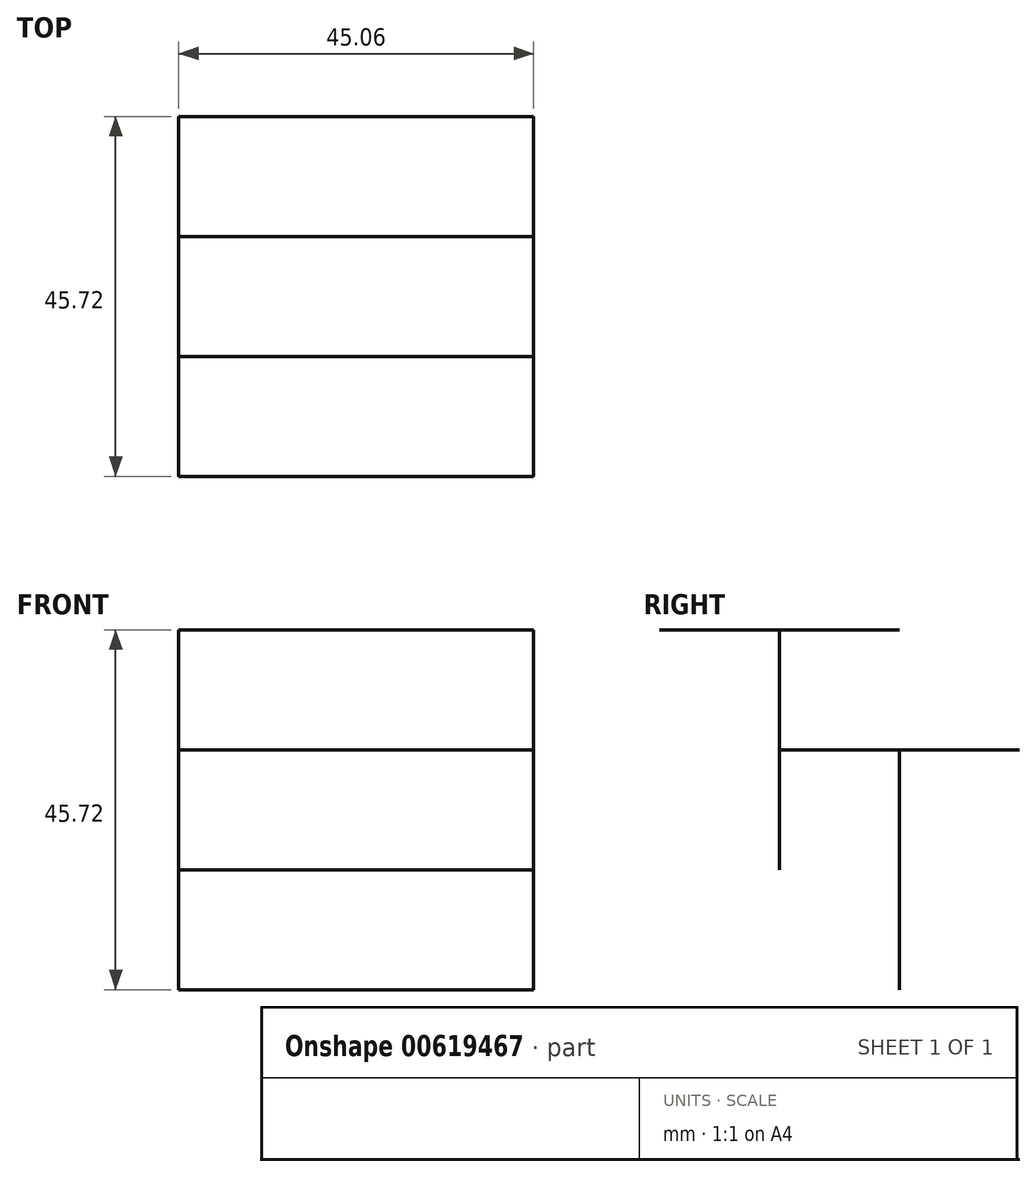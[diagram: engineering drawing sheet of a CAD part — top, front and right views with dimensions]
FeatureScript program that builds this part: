
annotation { "Feature Type Name" : "Feature", "Feature Type Description" : "" }
export const myFeature = defineFeature(function(context is Context, id is Id, definition is map)
    precondition{}
    {
        {
            var Q0;
            Q0=qCreatedBy(makeId("Front.planeOp"),FACE);
            var sketch = newSketch(context, id + "F0", { "sketchPlane" : qUnion([Q0])});
            skLineSegment(sketch, "E0.bottom", {"start": v(-22.53, 0) * mm, "end": v(22.53, 0) * mm});
            skSolve(sketch);
        }
        {
            var Q0;
            Q0=sQuery(id+"F0.wireOp",EDGE,"E0.bottom");
            extrude(context, id + "F1", {"bodyType" : ToolBodyType.SURFACE, "surfaceEntities" : qUnion([Q0]), "depth" : 30.48 * mm, "offsetDistance" : 30.48 * mm});
        }
        {
            var Q0;
            Q0=makeQuery(id+"F1.opExtrude","SWEPT_FACE",FACE,{"disambiguationData":[OSD([sQuery(id+"F0.wireOp",EDGE,"E0.bottom")])]});
            var sketch = newSketch(context, id + "F2", { "sketchPlane" : qUnion([Q0])});
            skLineSegment(sketch, "E1.bottom", {"start": v(-22.53, 15.24) * mm, "end": v(22.53, 15.24) * mm});
            skSolve(sketch);
        }
        {
            var Q0;
            Q0=sQuery(id+"F2.wireOp",EDGE,"E1.bottom");
            extrude(context, id + "F3", {"bodyType" : ToolBodyType.SURFACE, "surfaceEntities" : qUnion([Q0]), "depth" : 30.48 * mm, "offsetDistance" : 30.48 * mm});
        }
        {
            var Q0;
            Q0=makeQuery(id+"F3.opExtrude","SWEPT_FACE",FACE,{"disambiguationData":[OSD([sQuery(id+"F2.wireOp",EDGE,"E1.bottom")])]});
            var sketch = newSketch(context, id + "F4", { "sketchPlane" : qUnion([Q0])});
            skLineSegment(sketch, "E2.bottom", {"start": v(-22.53, -15.24) * mm, "end": v(22.53, -15.24) * mm});
            skSolve(sketch);
        }
        {
            var Q0;
            Q0=sQuery(id+"F4.wireOp",EDGE,"E2.bottom");
            extrude(context, id + "F5", {"bodyType" : ToolBodyType.SURFACE, "surfaceEntities" : qUnion([Q0]), "depth" : 30.48 * mm, "offsetDistance" : 30.48 * mm});
        }
        {
            var Q0;
            Q0=makeQuery(id+"F5.opExtrude","SWEPT_FACE",FACE,{"disambiguationData":[OSD([sQuery(id+"F4.wireOp",EDGE,"E2.bottom")])]});
            var sketch = newSketch(context, id + "F6", { "sketchPlane" : qUnion([Q0])});
            skLineSegment(sketch, "E3.bottom", {"start": v(-22.53, 0) * mm, "end": v(22.53, 0) * mm});
            skSolve(sketch);
        }
        {
            var Q0;
            Q0=sQuery(id+"F6.wireOp",EDGE,"E3.bottom");
            extrude(context, id + "F7", {"bodyType" : ToolBodyType.SURFACE, "surfaceEntities" : qUnion([Q0]), "depth" : 30.48 * mm, "offsetDistance" : 30.48 * mm});
        }
    });
